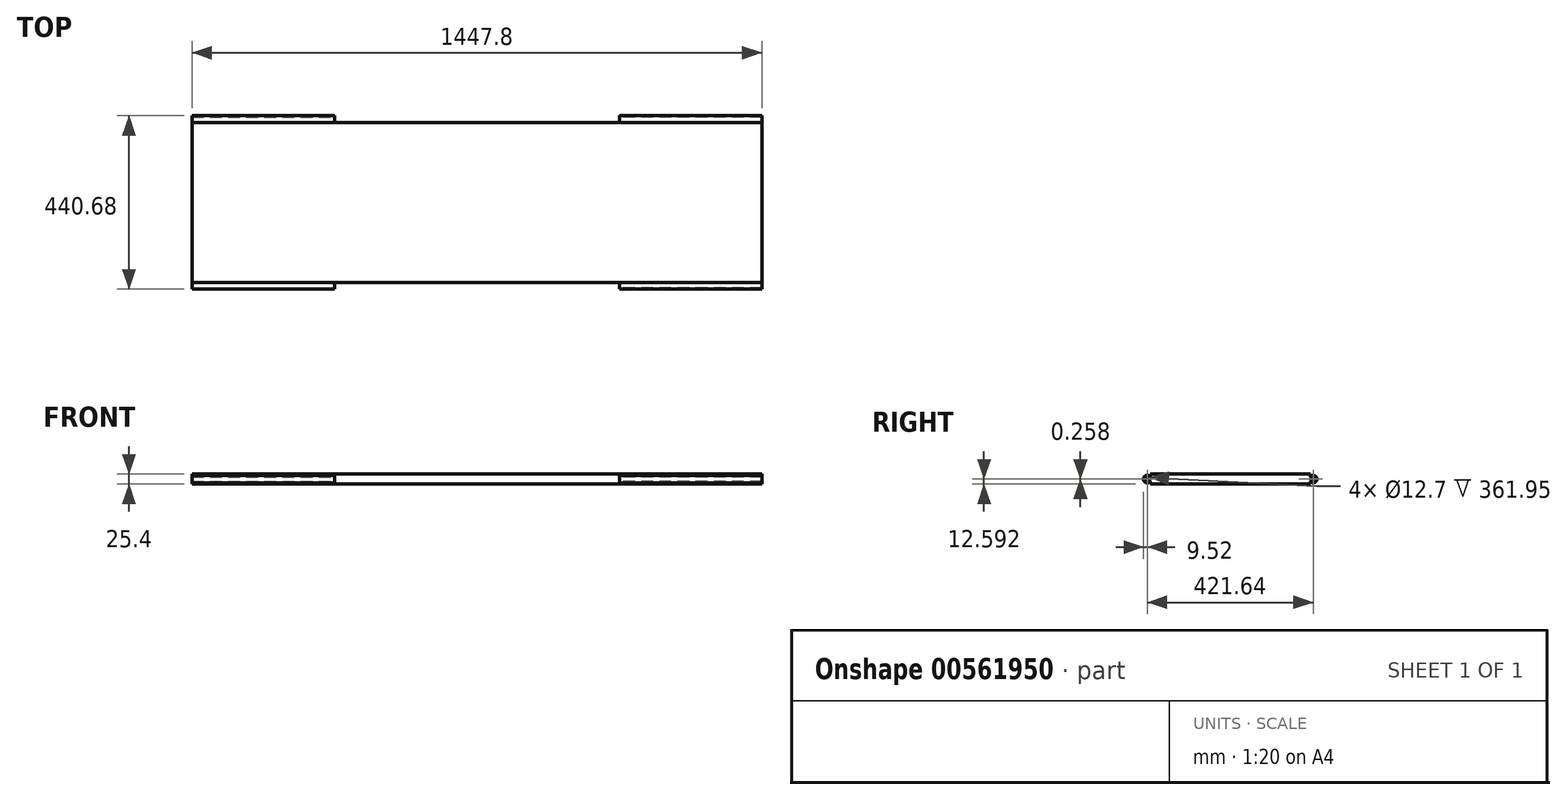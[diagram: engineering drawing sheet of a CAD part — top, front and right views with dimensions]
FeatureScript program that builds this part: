
annotation { "Feature Type Name" : "Feature", "Feature Type Description" : "" }
export const myFeature = defineFeature(function(context is Context, id is Id, definition is map)
    precondition{}
    {
        {
            var Q0;
            Q0=qCreatedBy(makeId("Top.planeOp"),FACE);
            var sketch = newSketch(context, id + "F0", { "sketchPlane" : qUnion([Q0])});
            skLineSegment(sketch, "E0.bottom", {"start": v(-723.9, 203.2) * mm, "end": v(723.9, 203.2) * mm});
            skLineSegment(sketch, "E0.top", {"start": v(-723.9, -203.2) * mm, "end": v(723.9, -203.2) * mm});
            skLineSegment(sketch, "E0.left", {"start": v(-723.9, 203.2) * mm, "end": v(-723.9, -203.2) * mm});
            skLineSegment(sketch, "E0.right", {"start": v(723.9, 203.2) * mm, "end": v(723.9, -203.2) * mm});
            skPoint(sketch, "E0.middle", {"position": v(0, 0) * mm});
            skSolve(sketch);
        }
        {
            var Q0;
            Q0=qCreatedBy(makeId("Right.planeOp"),FACE);
            cPlane(context, id + "F1", {"entities" : qUnion([Q0]), "cplaneType" : CPlaneType.OFFSET, "offset" : 361.95 * mm, "width" : 152.4 * mm, "height" : 152.4 * mm});
        }
        {
            var Q0;
            Q0=qCreatedBy(makeId("Right.planeOp"),FACE);
            cPlane(context, id + "F2", {"entities" : qUnion([Q0]), "cplaneType" : CPlaneType.OFFSET, "offset" : 361.95 * mm, "oppositeDirection" : true, "width" : 152.4 * mm, "height" : 152.4 * mm});
        }
        {
            var Q0;
            Q0=qCreatedBy(id+"F1.planeOp",FACE);
            var sketch = newSketch(context, id + "F3", { "sketchPlane" : qUnion([Q0])});
            skCircle(sketch, "E1", {"center": v(210.82, 0) * mm, "radius": 9.53 * mm});
            skCircle(sketch, "E2", {"center": v(210.82, 0) * mm, "radius": 6.35 * mm});
            skCircle(sketch, "E3", {"center": v(-210.82, -0.1) * mm, "radius": 9.53 * mm});
            skCircle(sketch, "E4", {"center": v(-210.82, -0.1) * mm, "radius": 6.35 * mm});
            skSolve(sketch);
        }
        {
            var Q0;
            Q0=qCreatedBy(id+"F2.planeOp",FACE);
            var sketch = newSketch(context, id + "F4", { "sketchPlane" : qUnion([Q0])});
            skCircle(sketch, "E5", {"center": v(210.82, 0) * mm, "radius": 9.53 * mm});
            skCircle(sketch, "E6", {"center": v(210.82, 0) * mm, "radius": 6.35 * mm});
            skCircle(sketch, "E7", {"center": v(-210.82, 0.15) * mm, "radius": 9.53 * mm});
            skCircle(sketch, "E8", {"center": v(-210.82, 0.15) * mm, "radius": 6.35 * mm});
            skSolve(sketch);
        }
        {
            var Q0;
            Q0=makeQuery(id+"F0.imprint","IMPRINT",FACE,{"disambiguationData":[TD([[makeQuery(id+"F0.imprint","IMPRINT",EDGE,{"derivedFrom":sQuery(id+"F0.wireOp",EDGE,"E0.bottom")}),-1.0]])]});
            extrude(context, id + "F5", {"entities" : qUnion([Q0]), "depth" : 25.4 * mm, "offsetDistance" : 25.4 * mm, "symmetric" : true});
        }
        {
            var Q0;
            Q0=makeQuery(id+"F4.imprint","IMPRINT",FACE,{"disambiguationData":[TD([[makeQuery(id+"F4.imprint","IMPRINT",EDGE,{"derivedFrom":sQuery(id+"F4.wireOp",EDGE,"E5")}),1.0]])]});
            extrude(context, id + "F6", {"entities" : qUnion([Q0]), "operationType" : NewBodyOperationType.ADD, "oppositeDirection" : true, "depth" : 361.95 * mm, "offsetDistance" : 25.4 * mm});
        }
        {
            var Q0;
            Q0=makeQuery(id+"F3.imprint","IMPRINT",FACE,{"disambiguationData":[TD([[makeQuery(id+"F3.imprint","IMPRINT",EDGE,{"derivedFrom":sQuery(id+"F3.wireOp",EDGE,"E1")}),1.0]])]});
            extrude(context, id + "F7", {"entities" : qUnion([Q0]), "operationType" : NewBodyOperationType.ADD, "depth" : 361.95 * mm, "offsetDistance" : 25.4 * mm});
        }
        {
            var Q0;
            Q0=makeQuery(id+"F4.imprint","IMPRINT",FACE,{"disambiguationData":[TD([[makeQuery(id+"F4.imprint","IMPRINT",EDGE,{"derivedFrom":sQuery(id+"F4.wireOp",EDGE,"E7")}),1.0]])]});
            extrude(context, id + "F8", {"entities" : qUnion([Q0]), "operationType" : NewBodyOperationType.ADD, "oppositeDirection" : true, "depth" : 361.95 * mm, "offsetDistance" : 25.4 * mm});
        }
        {
            var Q0;
            Q0=makeQuery(id+"F3.imprint","IMPRINT",FACE,{"disambiguationData":[TD([[makeQuery(id+"F3.imprint","IMPRINT",EDGE,{"derivedFrom":sQuery(id+"F3.wireOp",EDGE,"E3")}),1.0]])]});
            extrude(context, id + "F9", {"entities" : qUnion([Q0]), "operationType" : NewBodyOperationType.ADD, "depth" : 361.95 * mm, "offsetDistance" : 25.4 * mm});
        }
    });
